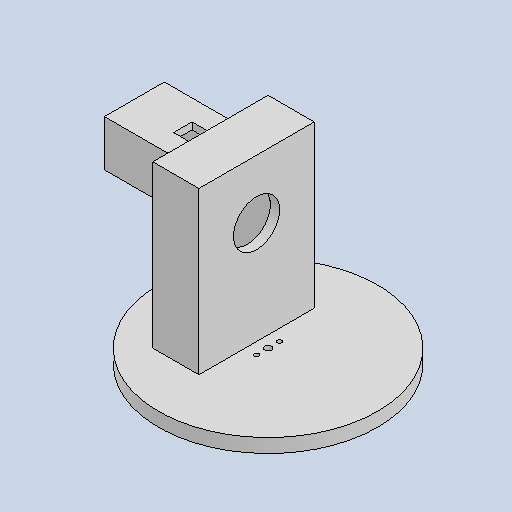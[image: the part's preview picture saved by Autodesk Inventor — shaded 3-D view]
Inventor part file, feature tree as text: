
AUTODESK INVENTOR PART (.ipt)
format: ipt  version: 2022 (Build 260153000, 153)  size: 299,520 bytes
history: native  units: in
note: dims shown in document units (in); Inventor stores cm internally (conversion verified against a paired STEP export)
features: extrude x16, sketch x16, thread x4
ambient origin geometry x8: Origin, YZ Plane, XZ Plane, XY Plane, X Axis, Y Axis, Z Axis, Center Point
bodies: Solid1 (feature_tree)
feature tree (36):
  extrude  "Extrusion1"  Depth=0.2362in TaperAngle=0.0deg
  extrude  "Extrusion2"  Depth=0.7874in
  extrude  "Extrusion3"  Depth=0.9237in TaperAngle=0.0deg
  extrude  "Extrusion4"  Depth=0.3937in
  extrude  "Extrusion5"  Depth=1.9685in
  extrude  "Extrusion6"  Depth=2.7559in TaperAngle=0.0deg
  thread  "Thread1"  [1 undecoded]
  thread  "Thread2"  [1 undecoded]
  thread  "Thread3"  [1 undecoded]
  thread  "Thread4"  [1 undecoded]
  extrude  "Extrusion7"  Depth=0.6299in TaperAngle=0.0deg
  extrude  "Extrusion8"  Depth=0.2362in
  extrude  "Extrusion9"  Depth=0.1024in
  extrude  "Extrusion10"  Depth=0.1181in
  extrude  "Extrusion11"  Depth=0.1969in
  extrude  "Extrusion12"  Depth=0.1063in
  extrude  "Extrusion13"  Depth=0.1063in
  extrude  "Extrusion14"  Depth=0.3937in TaperAngle=0.0deg
  extrude  "Extrusion15"  Depth=0.3937in TaperAngle=0.0deg
  extrude  "Extrusion16"  Depth=0.6693in
  sketch  "Sketch1"  dims[d0=3.7402in d1=0.2362in d2=0.0in]
  sketch  "Sketch2"  dims[d3=0.7874in d4=0.0787in]
  sketch  "Sketch4"  dims[d5=0.0787in d6=0.9237in d7=0.0in]
  sketch  "Sketch5"  dims[d9=0.3937in d10=0.9843in]
  sketch  "Sketch6"  dims[d11=0.5906in d12=1.9685in]
  sketch  "Sketch7"  dims[d13=0.7874in d14=2.7559in d15=0.0in d16=0.3937in d17=0.7874in d18=0.7874in d19=0.7874in]
  sketch  "Sketch8"  dims[d20=1.5945in d21=0.6299in d22=0.0in]
  sketch  "Sketch9"  dims[d23=0.2362in d24=0.2362in]
  sketch  "Sketch10"  dims[d25=0.2362in d26=0.0in d27=0.1024in]
  sketch  "Sketch11"  dims[d28=0.1181in d29=0.1181in]
  sketch  "Sketch12"  dims[d30=0.1969in d31=0.1969in]
  sketch  "Sketch13"  dims[d32=0.1063in d33=0.1063in]
  sketch  "Sketch16"  dims[d34=0.1063in d35=0.1063in]
  sketch  "Sketch17"  dims[d36=0.3937in d37=0.0in d38=0.3937in d39=0.0in]
  sketch  "Sketch19"  dims[d40=0.3937in d41=0.0in d42=0.3937in d43=0.0in]
  sketch  "Sketch20"  dims[d44=0.3937in d45=0.0in d46=0.6693in d47=0.7874in d48=0.6063in d49=0.0in d50=0.1181in d51=0.6063in d52=0.0in d53=0.2047in d54=0.1437in d55=0.0in d56=0.3937in d57=0.0in d58=0.1181in d59=0.2362in d60=0.2362in d61=0.4724in d62=0.0in d63=0.7874in d64=0.1181in d65=0.1181in d66=0.7874in d67=0.1181in d68=1.1811in d69=0.0in d70=0.1181in d71=0.1181in d72=0.1181in d73=0.0in d74=0.1181in d75=0.7874in d76=0.0in d77=0.4724in d78=0.1575in d79=0.1575in d80=0.1575in d81=0.0in d82=0.1181in d83=0.0in]
note: 4 required parameter values undecoded (feature->parameter linkage not recoverable at this tier; creation-order binding heuristic only, values carry confidence <= 0.55)
